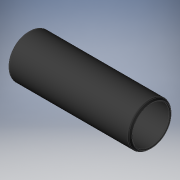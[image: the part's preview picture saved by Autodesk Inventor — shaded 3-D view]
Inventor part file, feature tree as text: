
AUTODESK INVENTOR PART (.ipt)
format: ipt  version: 2019 (Build 230136000, 136)  size: 167,936 bytes
history: native  units: in
note: dims shown in document units (in); Inventor stores cm internally (conversion verified against a paired STEP export)
features: other x42, revolve x1, sketch x1
ambient origin geometry x8: Origin, YZ Plane, XZ Plane, XY Plane, X Axis, Y Axis, Z Axis, Center Point
bodies: Solid1 (feature_tree)
feature tree (44):
  revolve  "Revolution1"  [1 undecoded]
  other  "cp1_XY"
  other  "cp1_YZ"
  other  "cp1_ZX"
  other  "cp1_X"
  other  "cp1_Y"
  other  "cp1_Z"
  other  "cp1_Center"
  other  "cp2_XY"
  other  "cp2_YZ"
  other  "cp2_ZX"
  other  "cp2_X"
  other  "cp2_Y"
  other  "cp2_Z"
  other  "cp2_Center"
  other  "cp3_XY"
  other  "cp3_YZ"
  other  "cp3_ZX"
  other  "cp3_X"
  other  "cp3_Y"
  other  "cp3_Z"
  other  "cp3_Center"
  other  "cp4_XY"
  other  "cp4_YZ"
  other  "cp4_ZX"
  other  "cp4_X"
  other  "cp4_Y"
  other  "cp4_Z"
  other  "cp4_Center"
  other  "tube_front_XY"
  other  "tube_front_YZ"
  other  "tube_front_ZX"
  other  "tube_front_X"
  other  "tube_front_Y"
  other  "tube_front_Z"
  other  "tube_front_Center"
  other  "tube_rear_XY"
  other  "tube_rear_YZ"
  other  "tube_rear_ZX"
  other  "tube_rear_X"
  other  "tube_rear_Y"
  other  "tube_rear_Z"
  other  "tube_rear_Center"
  sketch  "Sketch_1"  dims[d0=360.0deg]
note: 1 required parameter value undecoded (feature->parameter linkage not recoverable at this tier; creation-order binding heuristic only, values carry confidence <= 0.55)
